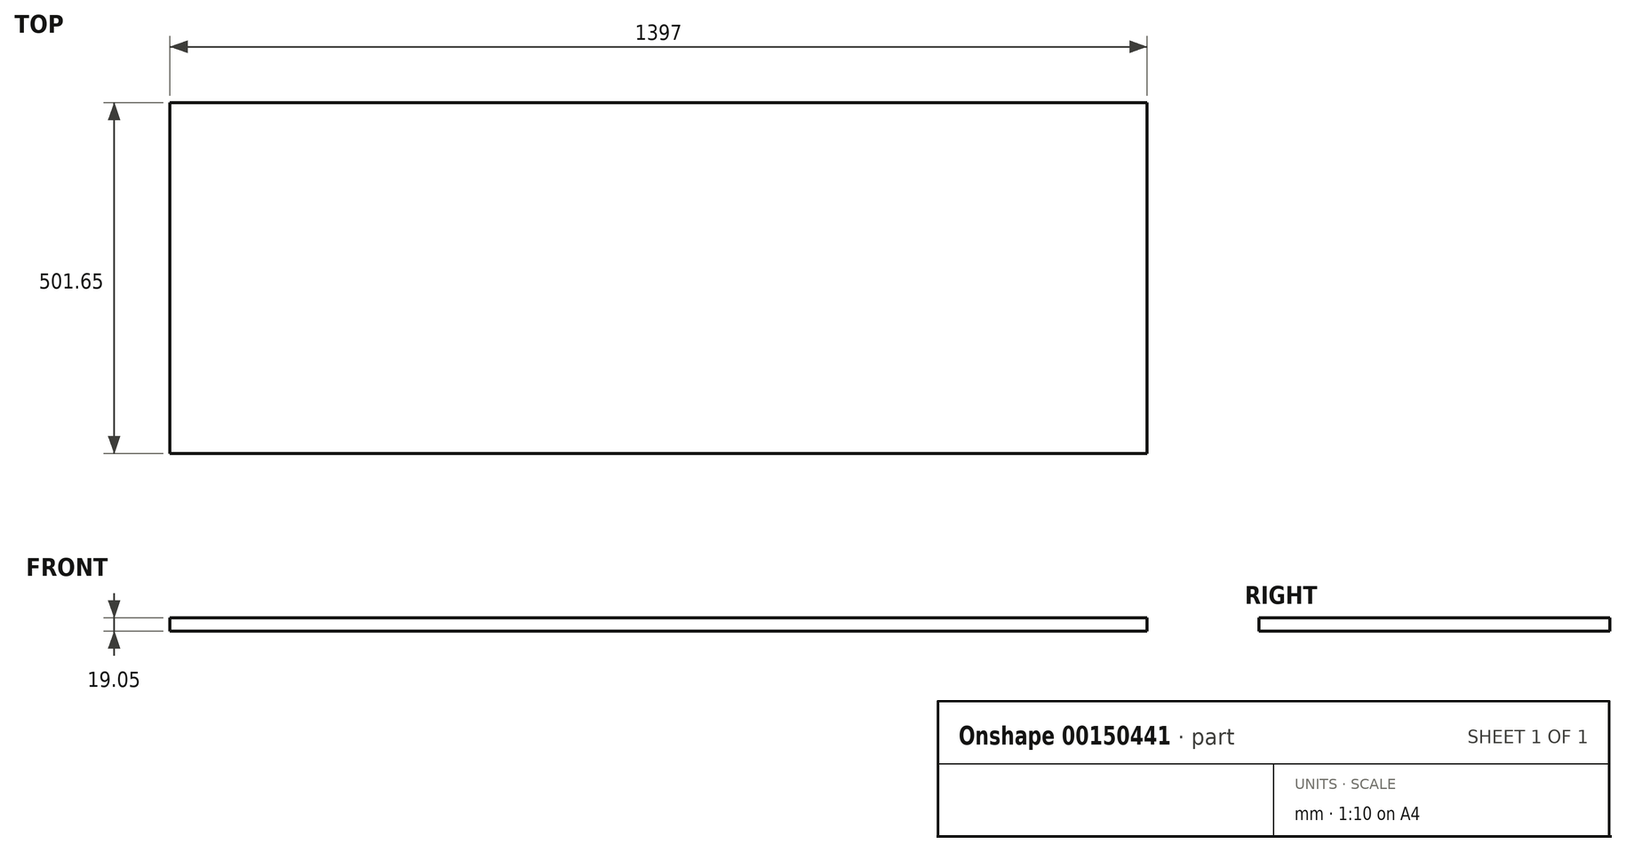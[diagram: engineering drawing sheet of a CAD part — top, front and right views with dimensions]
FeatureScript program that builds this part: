
annotation { "Feature Type Name" : "Feature", "Feature Type Description" : "" }
export const myFeature = defineFeature(function(context is Context, id is Id, definition is map)
    precondition{}
    {
        {
            var Q0;
            Q0=qCreatedBy(makeId("Top.planeOp"),FACE);
            var sketch = newSketch(context, id + "F0", { "sketchPlane" : qUnion([Q0])});
            skLineSegment(sketch, "E0.bottom", {"start": v(-698.5, 0) * mm, "end": v(698.5, 0) * mm});
            skLineSegment(sketch, "E0.top", {"start": v(-698.5, -501.65) * mm, "end": v(698.5, -501.65) * mm});
            skLineSegment(sketch, "E0.left", {"start": v(-698.5, 0) * mm, "end": v(-698.5, -501.65) * mm});
            skLineSegment(sketch, "E0.right", {"start": v(698.5, 0) * mm, "end": v(698.5, -501.65) * mm});
            skSolve(sketch);
        }
        {
            var Q0;
            Q0 = qSketchRegion(id + "F0", true);
            extrude(context, id + "F1", {"entities" : qUnion([Q0]), "oppositeDirection" : true, "depth" : 19.05 * mm});
        }
    });
